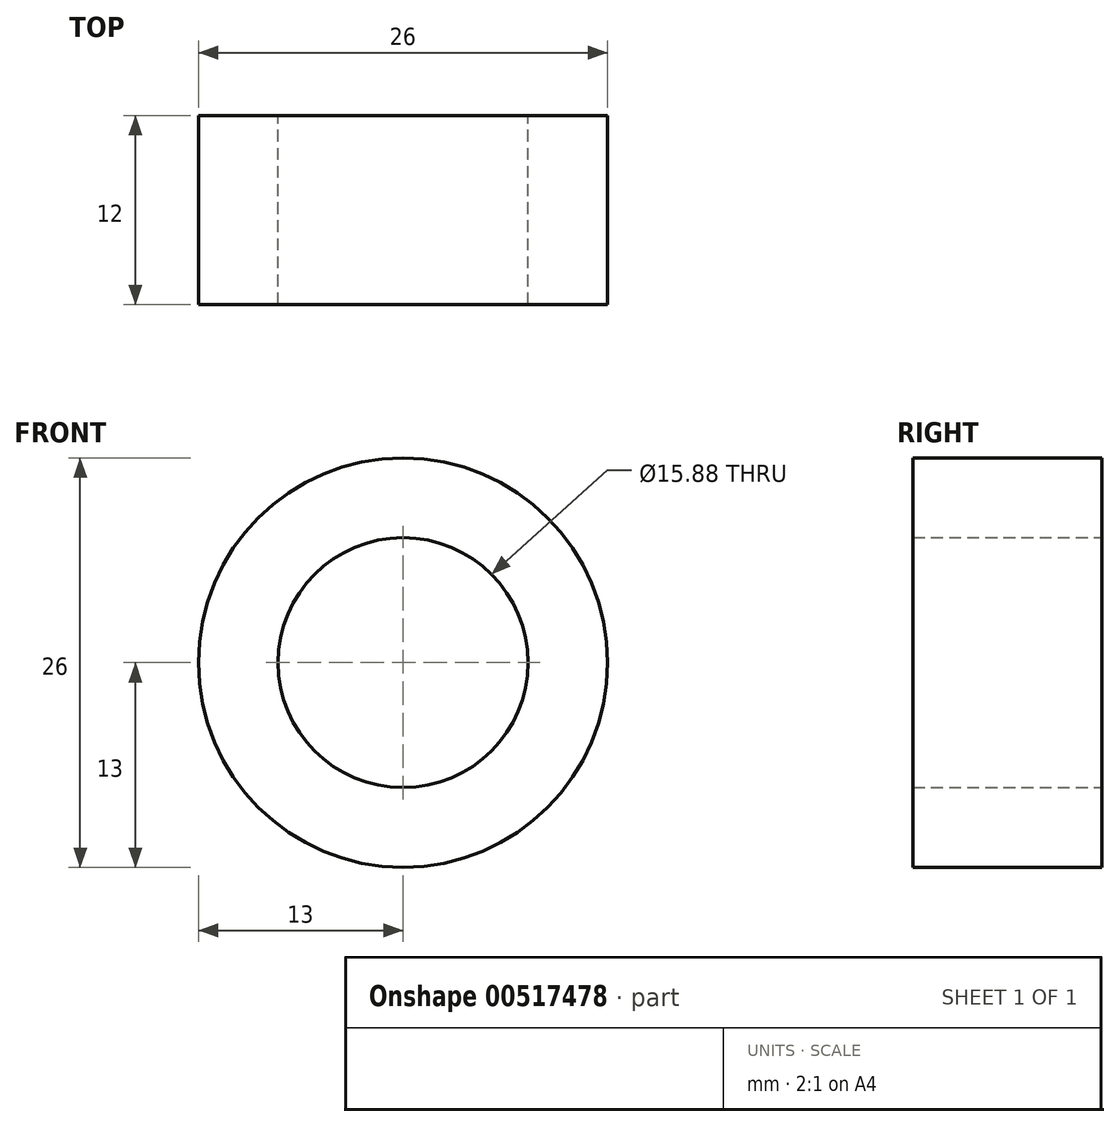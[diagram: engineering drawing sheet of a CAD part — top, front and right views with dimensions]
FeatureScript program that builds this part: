
annotation { "Feature Type Name" : "Feature", "Feature Type Description" : "" }
export const myFeature = defineFeature(function(context is Context, id is Id, definition is map)
    precondition{}
    {
        {
            var Q0;
            Q0=qCreatedBy(makeId("Front.planeOp"),FACE);
            var sketch = newSketch(context, id + "F0", { "sketchPlane" : qUnion([Q0])});
            skCircle(sketch, "E0", {"center": v(0, 0) * mm, "radius": 13 * mm});
            skCircle(sketch, "E1", {"center": v(0, 0) * mm, "radius": 7.94 * mm});
            skSolve(sketch);
        }
        {
            var Q0;
            Q0 = qSketchRegion(id + "F0", true);
            extrude(context, id + "F1", {"entities" : qUnion([Q0]), "depth" : 12 * mm, "offsetDistance" : 25.4 * mm});
        }
    });
